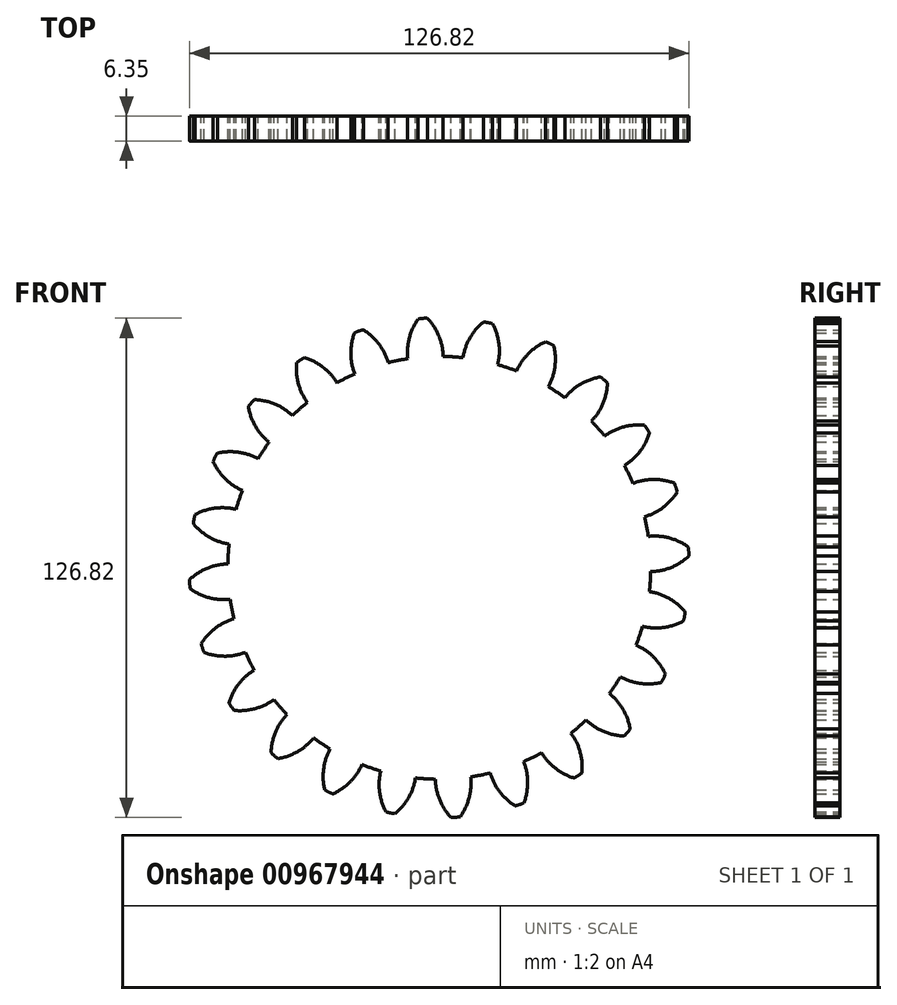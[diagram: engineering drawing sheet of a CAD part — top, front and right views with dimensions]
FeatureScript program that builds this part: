
annotation { "Feature Type Name" : "Feature", "Feature Type Description" : "" }
export const myFeature = defineFeature(function(context is Context, id is Id, definition is map)
    precondition{}
    {
        {
            var Q0;
            Q0=qCreatedBy(makeId("Front.planeOp"),FACE);
            var sketch = newSketch(context, id + "F0", { "sketchPlane" : qUnion([Q0])});
            skCircle(sketch, "E0", {"center": v(0, 0) * mm, "radius": 53.72 * mm});
            skCircle(sketch, "E1", {"center": v(0, 0) * mm, "radius": 58.67 * mm, "construction": true});
            skCircle(sketch, "E2", {"center": v(0, 0) * mm, "radius": 63.5 * mm, "construction": true});
            skLineSegment(sketch, "E3", {"start": v(0, 0) * mm, "end": v(0, 97.66) * mm, "construction": true});
            skLineSegment(sketch, "E4", {"start": v(0, 0) * mm, "end": v(-6.36, 97.1) * mm, "construction": true});
            skLineSegment(sketch, "E5", {"start": v(0, 58.67) * mm, "end": v(-101.23, 58.67) * mm, "construction": true});
            skLineSegment(sketch, "E6", {"start": v(0, 58.67) * mm, "end": v(-101.2, 21.84) * mm, "construction": true});
            skCircle(sketch, "E7", {"center": v(0, 58.67) * mm, "radius": 14.6 * mm, "construction": true});
            skCircle(sketch, "E8", {"center": v(0, 0) * mm, "radius": 55.14 * mm, "construction": true});
            skCircle(sketch, "E9", {"center": v(-13.63, 53.42) * mm, "radius": 14.6 * mm, "construction": true});
            skArc(sketch, "E10", {"start": v(0, 58.67) * mm, "mid": v(-1.26, 61.17) * mm, "end": v(-2.97, 63.4) * mm});
            skArc(sketch, "E11", {"start": v(0.97, 53.71) * mm, "mid": v(0.71, 56.24) * mm, "end": v(0, 58.67) * mm});
            skArc(sketch, "E12.MirrorCS", {"start": v(-7.66, 58.17) * mm, "mid": v(-6.73, 60.82) * mm, "end": v(-5.34, 63.24) * mm});
            skArc(sketch, "E13.MirrorCS", {"start": v(-7.98, 53.13) * mm, "mid": v(-8.05, 55.66) * mm, "end": v(-7.66, 58.17) * mm});
            skArc(sketch, "E14", {"start": v(-2.97, 63.4) * mm, "mid": v(-4.15, 63.38) * mm, "end": v(-5.34, 63.24) * mm});
            skSolve(sketch);
        }
        {
            var Q0;
            {var subQ0=sQuery(id+"F0.wireOp",EDGE,"E0");var subQ1=makeQuery(id+"F0.imprint","INTERSECT",VERTEX,{"derivedFrom":[subQ0,sQuery(id+"F0.wireOp",EDGE,"E11")]});Q0=makeQuery(id+"F0.imprint","IMPRINT",FACE,{"disambiguationData":[TD([[makeQuery(id+"F0.imprint","IMPRINT",EDGE,{"disambiguationData":[TD([[subQ1,-1.0]])],"derivedFrom":subQ0}),1.0]])]});}
            var Q1;
            Q1=makeQuery(id+"F0.imprint","IMPRINT",FACE,{"disambiguationData":[TD([[makeQuery(id+"F0.imprint","IMPRINT",EDGE,{"derivedFrom":sQuery(id+"F0.wireOp",EDGE,"E10")}),1.0]])]});
            extrude(context, id + "F1", {"entities" : qUnion([Q0, Q1]), "depth" : 6.35 * mm, "offsetDistance" : 25.4 * mm});
        }
        {
            var Q0;
            Q0=makeQuery(id+"F1.opExtrude","SWEPT_BODY",BODY,{"disambiguationData":[OSD([sQuery(id+"F0.wireOp",EDGE,"E0"),sQuery(id+"F0.wireOp",EDGE,"E10"),sQuery(id+"F0.wireOp",EDGE,"E11"),sQuery(id+"F0.wireOp",EDGE,"E12.MirrorCS"),sQuery(id+"F0.wireOp",EDGE,"E13.MirrorCS"),sQuery(id+"F0.wireOp",EDGE,"E14")])]});
            var Q1;
            Q1=makeQuery(id+"F1.opExtrude","CAP_EDGE",EDGE,{"disambiguationData":[OSD([sQuery(id+"F0.wireOp",EDGE,"E0")])],"isStart":false});
            circularPattern(context, id + "F2", {"operationType" : NewBodyOperationType.ADD, "entities" : qUnion([Q0]), "axis" : qUnion([Q1]), "angle" : 15 * degree, "instanceCount" : 24});
        }
    });
